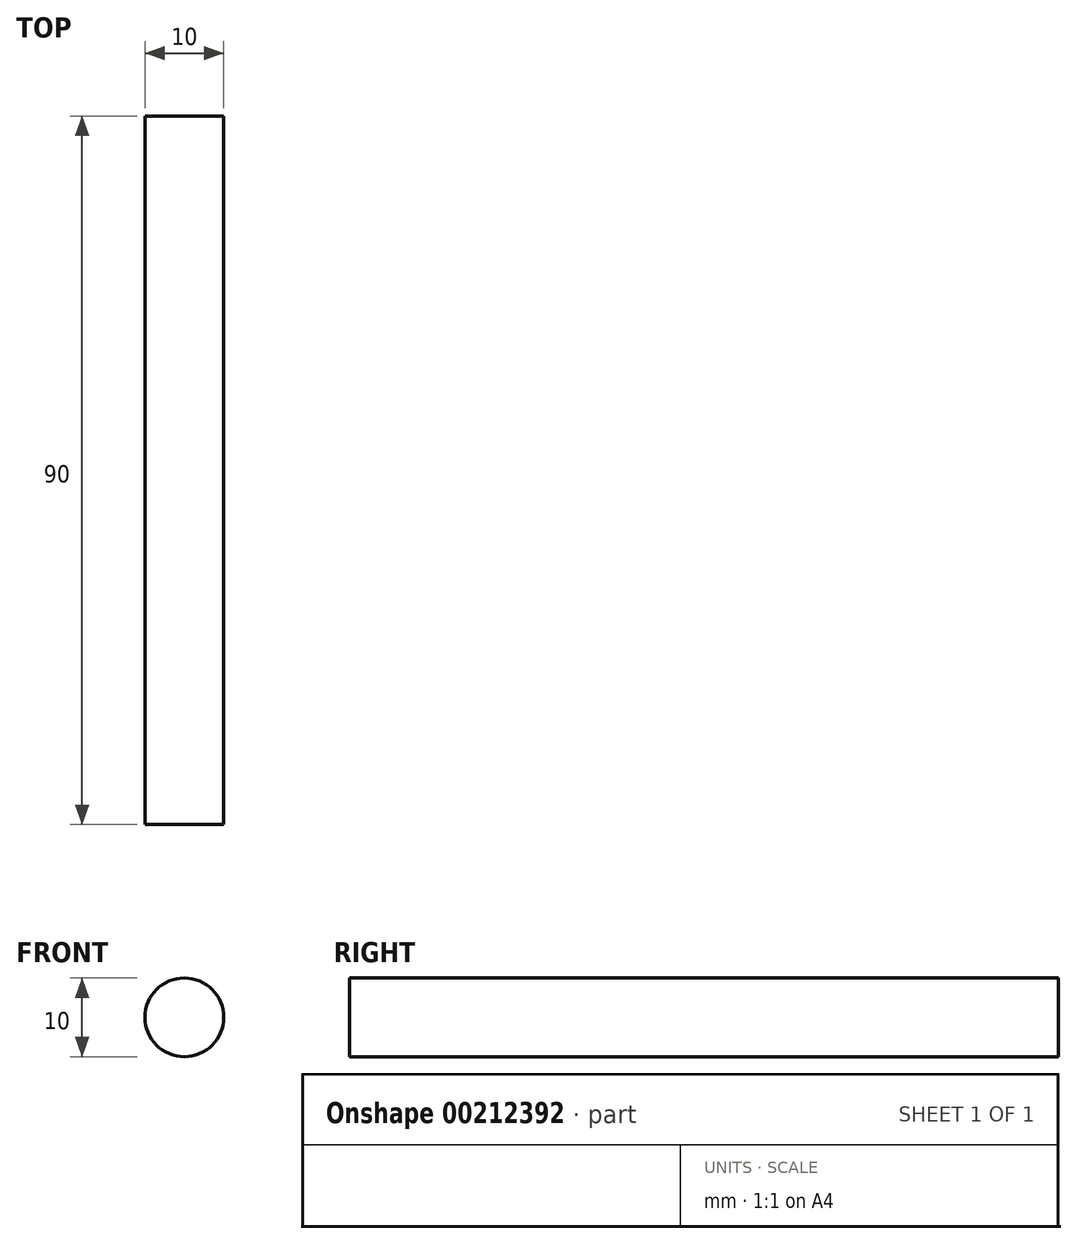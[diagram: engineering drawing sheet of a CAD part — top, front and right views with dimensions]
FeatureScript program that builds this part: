
annotation { "Feature Type Name" : "Feature", "Feature Type Description" : "" }
export const myFeature = defineFeature(function(context is Context, id is Id, definition is map)
    precondition{}
    {
        {
            var Q0;
            Q0=qCreatedBy(makeId("Front.planeOp"),FACE);
            var sketch = newSketch(context, id + "F0", { "sketchPlane" : qUnion([Q0])});
            skCircle(sketch, "E0", {"center": v(0, 0) * mm, "radius": 5 * mm});
            skSolve(sketch);
        }
        {
            var Q0;
            Q0=makeQuery(id+"F0.imprint","IMPRINT",FACE,{"disambiguationData":[TD([[makeQuery(id+"F0.imprint","IMPRINT",EDGE,{"derivedFrom":sQuery(id+"F0.wireOp",EDGE,"E0")}),1.0]])]});
            extrude(context, id + "F1", {"entities" : qUnion([Q0]), "depth" : 90 * mm});
        }
    });
